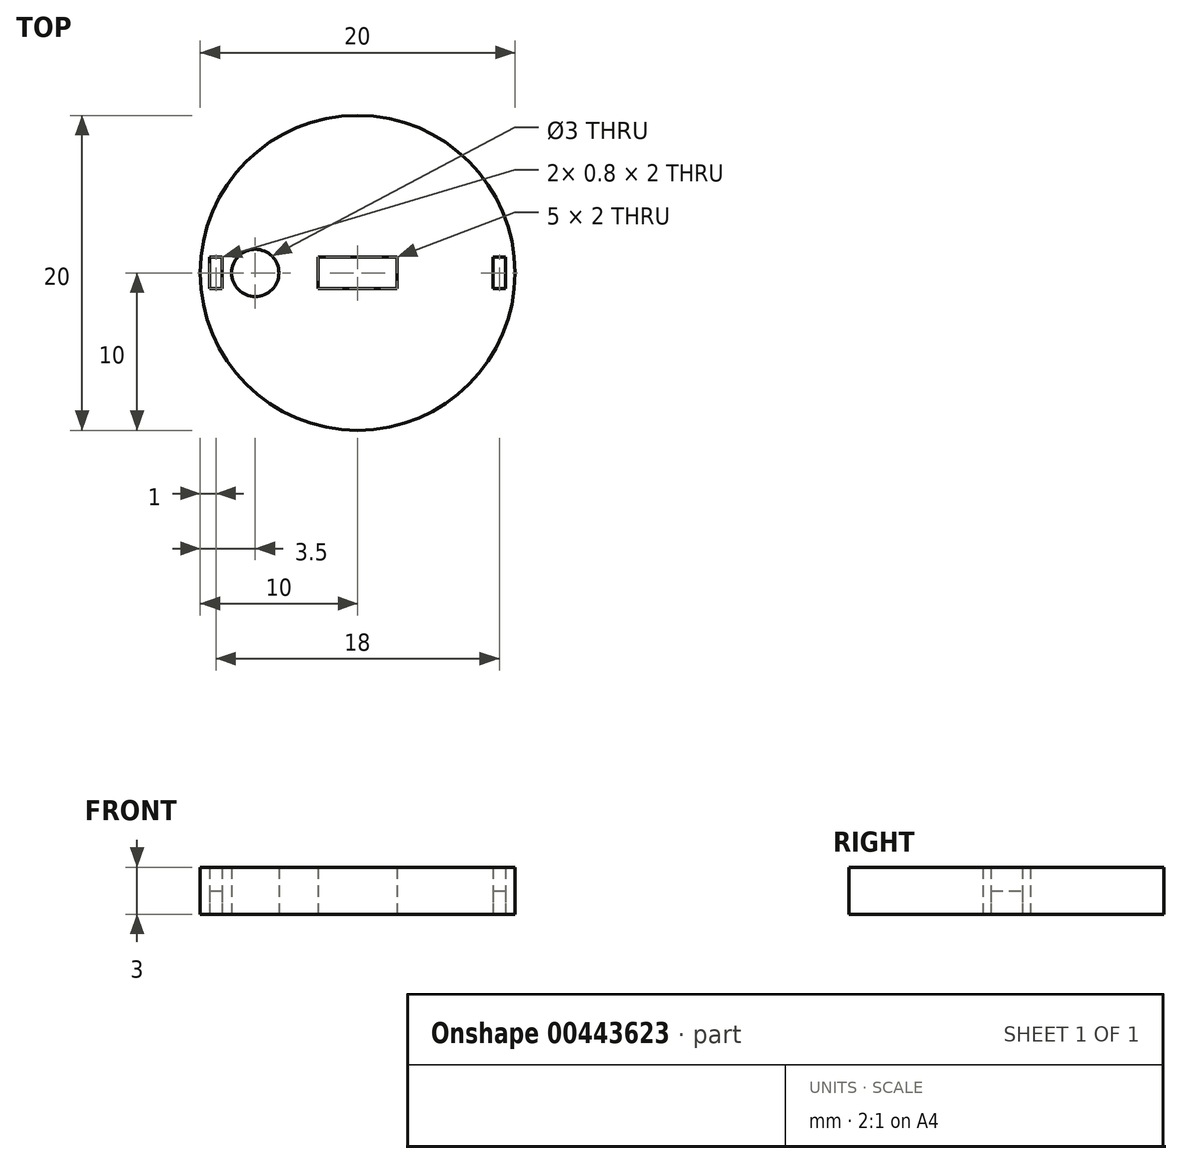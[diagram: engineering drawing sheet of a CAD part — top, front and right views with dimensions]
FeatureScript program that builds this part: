
annotation { "Feature Type Name" : "Feature", "Feature Type Description" : "" }
export const myFeature = defineFeature(function(context is Context, id is Id, definition is map)
    precondition{}
    {
        {
            var Q0;
            Q0=qCreatedBy(makeId("Top.planeOp"),FACE);
            var sketch = newSketch(context, id + "F0", { "sketchPlane" : qUnion([Q0])});
            skCircle(sketch, "E0", {"center": v(0, 0) * mm, "radius": 10 * mm});
            skCircle(sketch, "E1", {"center": v(-6.5, 0) * mm, "radius": 1.5 * mm});
            skLineSegment(sketch, "E2.bottom", {"start": v(-9.4, -1) * mm, "end": v(-8.6, -1) * mm});
            skLineSegment(sketch, "E2.top", {"start": v(-9.4, 1) * mm, "end": v(-8.6, 1) * mm});
            skLineSegment(sketch, "E2.left", {"start": v(-9.4, -1) * mm, "end": v(-9.4, 1) * mm});
            skLineSegment(sketch, "E2.right", {"start": v(-8.6, -1) * mm, "end": v(-8.6, 1) * mm});
            skLineSegment(sketch, "E3.bottom", {"start": v(8.6, -1) * mm, "end": v(9.4, -1) * mm});
            skLineSegment(sketch, "E3.top", {"start": v(8.6, 1) * mm, "end": v(9.4, 1) * mm});
            skLineSegment(sketch, "E3.left", {"start": v(8.6, -1) * mm, "end": v(8.6, 1) * mm});
            skLineSegment(sketch, "E3.right", {"start": v(9.4, -1) * mm, "end": v(9.4, 1) * mm});
            skLineSegment(sketch, "E4.bottom", {"start": v(-2.5, 1) * mm, "end": v(2.5, 1) * mm});
            skLineSegment(sketch, "E4.top", {"start": v(-2.5, -1) * mm, "end": v(2.5, -1) * mm});
            skLineSegment(sketch, "E4.left", {"start": v(-2.5, 1) * mm, "end": v(-2.5, -1) * mm});
            skLineSegment(sketch, "E4.right", {"start": v(2.5, 1) * mm, "end": v(2.5, -1) * mm});
            skSolve(sketch);
        }
        {
            var Q0;
            Q0=makeQuery(id+"F0.imprint","IMPRINT",FACE,{"disambiguationData":[TD([[makeQuery(id+"F0.imprint","IMPRINT",EDGE,{"derivedFrom":sQuery(id+"F0.wireOp",EDGE,"E0")}),1.0]])]});
            extrude(context, id + "F1", {"entities" : qUnion([Q0]), "depth" : 3 * mm});
        }
        {
            var Q0;
            Q0=makeQuery(id+"F0.imprint","IMPRINT",FACE,{"disambiguationData":[TD([[makeQuery(id+"F0.imprint","IMPRINT",EDGE,{"derivedFrom":sQuery(id+"F0.wireOp",EDGE,"E2.bottom")}),1.0]])]});
            var Q1;
            Q1=makeQuery(id+"F0.imprint","IMPRINT",FACE,{"disambiguationData":[TD([[makeQuery(id+"F0.imprint","IMPRINT",EDGE,{"derivedFrom":sQuery(id+"F0.wireOp",EDGE,"E3.bottom")}),1.0]])]});
            extrude(context, id + "F2", {"entities" : qUnion([Q0, Q1]), "depth" : 1.5 * mm});
        }
    });
